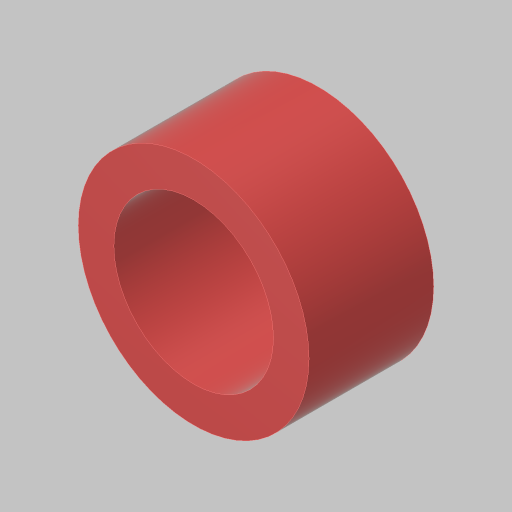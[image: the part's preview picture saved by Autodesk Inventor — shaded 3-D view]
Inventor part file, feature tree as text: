
AUTODESK INVENTOR PART (.ipt)
format: ipt  version: 2023.5 (Build 275446000, 446)  size: 111,616 bytes
history: native  units: in
note: dims shown in document units (in); Inventor stores cm internally (conversion verified against a paired STEP export)
features: extrude x1, sketch x1
ambient origin geometry x8: Origin, YZ Plane, XZ Plane, XY Plane, X Axis, Y Axis, Z Axis, Center Point
bodies: Solid1 (feature_tree)
feature tree (2):
  extrude  "Extrusion1"  Depth=0.4375in
  sketch  "Sketch1"  dims[d0=0.56in d1=0.125in d2=0.4375in d3=0.0in]
